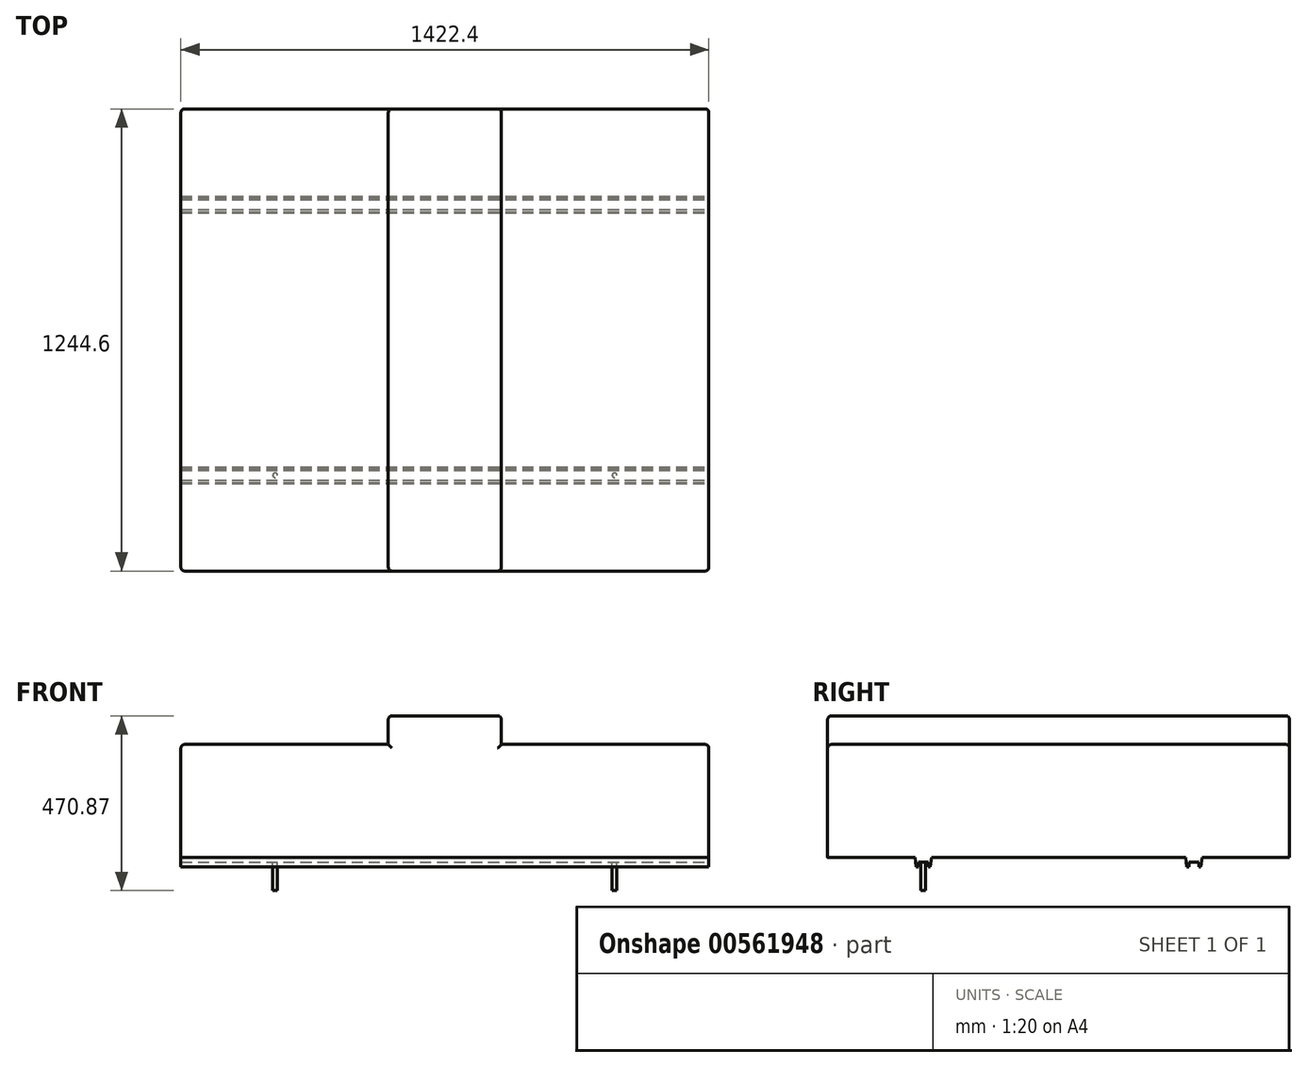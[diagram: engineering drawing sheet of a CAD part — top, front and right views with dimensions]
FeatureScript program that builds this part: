
annotation { "Feature Type Name" : "Feature", "Feature Type Description" : "" }
export const myFeature = defineFeature(function(context is Context, id is Id, definition is map)
    precondition{}
    {
        {
            var Q0;
            Q0=qCreatedBy(makeId("Front.planeOp"),FACE);
            var sketch = newSketch(context, id + "F0", { "sketchPlane" : qUnion([Q0])});
            skLineSegment(sketch, "E0.bottom", {"start": v(711.2, 152.4) * mm, "end": v(152.4, 152.4) * mm});
            skLineSegment(sketch, "E0.top", {"start": v(711.2, -152.4) * mm, "end": v(-711.2, -152.4) * mm});
            skLineSegment(sketch, "E0.left", {"start": v(711.2, 152.4) * mm, "end": v(711.2, -152.4) * mm});
            skLineSegment(sketch, "E0.right", {"start": v(-711.2, 152.4) * mm, "end": v(-711.2, -152.4) * mm});
            skPoint(sketch, "E0.middle", {"position": v(0, 0) * mm});
            skLineSegment(sketch, "E1.bottom", {"start": v(152.4, 229.57) * mm, "end": v(-152.4, 229.57) * mm});
            skLineSegment(sketch, "E1.top", {"start": v(152.4, 75.23) * mm, "end": v(-152.4, 75.23) * mm});
            skLineSegment(sketch, "E1.left", {"start": v(152.4, 229.57) * mm, "end": v(152.4, 75.23) * mm});
            skLineSegment(sketch, "E1.right", {"start": v(-152.4, 229.57) * mm, "end": v(-152.4, 75.23) * mm});
            skPoint(sketch, "E1.middle", {"position": v(0, 152.4) * mm});
            skLineSegment(sketch, "E2.trimOffspring", {"start": v(-152.4, 152.4) * mm, "end": v(-711.2, 152.4) * mm});
            skSolve(sketch);
        }
        {
            var Q0;
            Q0 = qSketchRegion(id + "F0", true);
            extrude(context, id + "F1", {"entities" : qUnion([Q0]), "depth" : 1244.6 * mm, "offsetDistance" : 25.4 * mm, "symmetric" : true});
        }
        {
            var Q0;
            Q0=makeQuery(id+"F1.opExtrude","SWEPT_EDGE",EDGE,{"disambiguationData":[OSD([sQuery(id+"F0.wireOp",EDGE,"E0.bottom"),sQuery(id+"F0.wireOp",EDGE,"E0.left")])]});
            var Q1;
            Q1=makeQuery(id+"F1.opExtrude","CAP_EDGE",EDGE,{"disambiguationData":[OSD([sQuery(id+"F0.wireOp",EDGE,"E0.bottom")])],"isStart":false});
            var Q2;
            Q2=makeQuery(id+"F1.opExtrude","CAP_EDGE",EDGE,{"disambiguationData":[OSD([sQuery(id+"F0.wireOp",EDGE,"E0.left")])],"isStart":false});
            var Q3;
            Q3=makeQuery(id+"F1.opExtrude","CAP_EDGE",EDGE,{"disambiguationData":[OSD([sQuery(id+"F0.wireOp",EDGE,"E0.bottom")])],"isStart":true});
            var Q4;
            Q4=makeQuery(id+"F1.opExtrude","CAP_EDGE",EDGE,{"disambiguationData":[OSD([sQuery(id+"F0.wireOp",EDGE,"E0.left")])],"isStart":true});
            var Q5;
            Q5=makeQuery(id+"F1.opExtrude","CAP_EDGE",EDGE,{"disambiguationData":[OSD([sQuery(id+"F0.wireOp",EDGE,"E1.bottom")])],"isStart":true});
            var Q6;
            Q6=makeQuery(id+"F1.opExtrude","CAP_EDGE",EDGE,{"disambiguationData":[OSD([sQuery(id+"F0.wireOp",EDGE,"E1.left")])],"isStart":true});
            var Q7;
            Q7=makeQuery(id+"F1.opExtrude","SWEPT_EDGE",EDGE,{"disambiguationData":[OSD([sQuery(id+"F0.wireOp",EDGE,"E1.bottom"),sQuery(id+"F0.wireOp",EDGE,"E1.left")])]});
            var Q8;
            Q8=makeQuery(id+"F1.opExtrude","CAP_EDGE",EDGE,{"disambiguationData":[OSD([sQuery(id+"F0.wireOp",EDGE,"E1.right")])],"isStart":true});
            var Q9;
            Q9=makeQuery(id+"F1.opExtrude","SWEPT_EDGE",EDGE,{"disambiguationData":[OSD([sQuery(id+"F0.wireOp",EDGE,"E1.bottom"),sQuery(id+"F0.wireOp",EDGE,"E1.right")])]});
            var Q10;
            Q10=makeQuery(id+"F1.opExtrude","CAP_EDGE",EDGE,{"disambiguationData":[OSD([sQuery(id+"F0.wireOp",EDGE,"E2.trimOffspring")])],"isStart":true});
            var Q11;
            Q11=makeQuery(id+"F1.opExtrude","CAP_EDGE",EDGE,{"disambiguationData":[OSD([sQuery(id+"F0.wireOp",EDGE,"E0.right")])],"isStart":true});
            var Q12;
            Q12=makeQuery(id+"F1.opExtrude","SWEPT_EDGE",EDGE,{"disambiguationData":[OSD([sQuery(id+"F0.wireOp",EDGE,"E0.right"),sQuery(id+"F0.wireOp",EDGE,"E2.trimOffspring")])]});
            var Q13;
            Q13=makeQuery(id+"F1.opExtrude","CAP_EDGE",EDGE,{"disambiguationData":[OSD([sQuery(id+"F0.wireOp",EDGE,"E0.right")])],"isStart":false});
            var Q14;
            Q14=makeQuery(id+"F1.opExtrude","CAP_EDGE",EDGE,{"disambiguationData":[OSD([sQuery(id+"F0.wireOp",EDGE,"E2.trimOffspring")])],"isStart":false});
            var Q15;
            Q15=makeQuery(id+"F1.opExtrude","CAP_EDGE",EDGE,{"disambiguationData":[OSD([sQuery(id+"F0.wireOp",EDGE,"E1.right")])],"isStart":false});
            var Q16;
            Q16=makeQuery(id+"F1.opExtrude","CAP_EDGE",EDGE,{"disambiguationData":[OSD([sQuery(id+"F0.wireOp",EDGE,"E1.bottom")])],"isStart":false});
            var Q17;
            Q17=makeQuery(id+"F1.opExtrude","CAP_EDGE",EDGE,{"disambiguationData":[OSD([sQuery(id+"F0.wireOp",EDGE,"E1.left")])],"isStart":false});
            fillet(context, id + "F2", {"entities" : qUnion([Q0, Q1, Q2, Q3, Q4, Q5, Q6, Q7, Q8, Q9, Q10, Q11, Q12, Q13, Q14, Q15, Q16, Q17]), "radius" : 10.16 * mm, "tangentPropagation" : true, "allowEdgeOverflow" : false});
        }
        {
            var Q0;
            Q0=makeQuery(id+"F1.opExtrude","SWEPT_FACE",FACE,{"disambiguationData":[OSD([sQuery(id+"F0.wireOp",EDGE,"E0.left")])]});
            var sketch = newSketch(context, id + "F3", { "sketchPlane" : qUnion([Q0])});
            skLineSegment(sketch, "E3", {"start": v(-386.72, -152.4) * mm, "end": v(-342.27, -152.4) * mm});
            skLineSegment(sketch, "E4", {"start": v(-364.5, -279.4) * mm, "end": v(-364.5, -152.4) * mm, "construction": true});
            skLineSegment(sketch, "E5", {"start": v(-383.54, -177.8) * mm, "end": v(-377.55, -177.8) * mm});
            skLineSegment(sketch, "E6", {"start": v(-386.72, -152.4) * mm, "end": v(-383.54, -177.8) * mm});
            skLineSegment(sketch, "E7", {"start": v(-342.27, -152.4) * mm, "end": v(-345.44, -177.8) * mm});
            skLineSegment(sketch, "E8.top", {"start": v(-377.55, -165.1) * mm, "end": v(-351.43, -165.1) * mm});
            skLineSegment(sketch, "E8.left", {"start": v(-377.55, -177.8) * mm, "end": v(-377.55, -165.1) * mm});
            skLineSegment(sketch, "E8.right", {"start": v(-351.43, -177.8) * mm, "end": v(-351.43, -165.1) * mm});
            skLineSegment(sketch, "E9.trimOffspring", {"start": v(-351.43, -177.8) * mm, "end": v(-345.44, -177.8) * mm});
            skLineSegment(sketch, "E10", {"start": v(342.27, -152.4) * mm, "end": v(386.72, -152.4) * mm});
            skLineSegment(sketch, "E11", {"start": v(345.44, -177.8) * mm, "end": v(351.43, -177.8) * mm});
            skLineSegment(sketch, "E12", {"start": v(342.27, -152.4) * mm, "end": v(345.44, -177.8) * mm});
            skLineSegment(sketch, "E13", {"start": v(386.72, -152.4) * mm, "end": v(383.54, -177.8) * mm});
            skLineSegment(sketch, "E14.top", {"start": v(351.43, -165.1) * mm, "end": v(377.55, -165.1) * mm});
            skLineSegment(sketch, "E14.left", {"start": v(351.43, -177.8) * mm, "end": v(351.43, -165.1) * mm});
            skLineSegment(sketch, "E14.right", {"start": v(377.55, -177.8) * mm, "end": v(377.55, -165.1) * mm});
            skLineSegment(sketch, "E15.trimOffspring", {"start": v(377.55, -177.8) * mm, "end": v(383.54, -177.8) * mm});
            skSolve(sketch);
        }
        {
            var Q0;
            Q0 = qSketchRegion(id + "F3", true);
            extrude(context, id + "F4", {"entities" : qUnion([Q0]), "operationType" : NewBodyOperationType.ADD, "oppositeDirection" : true, "depth" : 1422.4 * mm, "offsetDistance" : 25.4 * mm});
        }
        {
            var Q0;
            Q0=makeQuery(id+"F4.opExtrude","SWEPT_FACE",FACE,{"disambiguationData":[OSD([sQuery(id+"F3.wireOp",EDGE,"E8.top")])]});
            var sketch = newSketch(context, id + "F5", { "sketchPlane" : qUnion([Q0])});
            skLineSegment(sketch, "E16", {"start": v(-711.2, 364.5) * mm, "end": v(711.2, 364.5) * mm, "construction": true});
            skPoint(sketch, "E17.endSnap0", {"position": v(0, 377.55) * mm});
            skLineSegment(sketch, "E18", {"start": v(0, 542.82) * mm, "end": v(0, 0) * mm, "construction": true});
            skCircle(sketch, "E19", {"center": v(457.2, 364.5) * mm, "radius": 6.35 * mm});
            skCircle(sketch, "E20", {"center": v(-457.2, 364.5) * mm, "radius": 6.35 * mm});
            skSolve(sketch);
        }
        {
            var Q0;
            Q0 = qSketchRegion(id + "F5", true);
            extrude(context, id + "F6", {"entities" : qUnion([Q0]), "operationType" : NewBodyOperationType.ADD, "depth" : 76.2 * mm, "offsetDistance" : 25.4 * mm});
        }
    });
